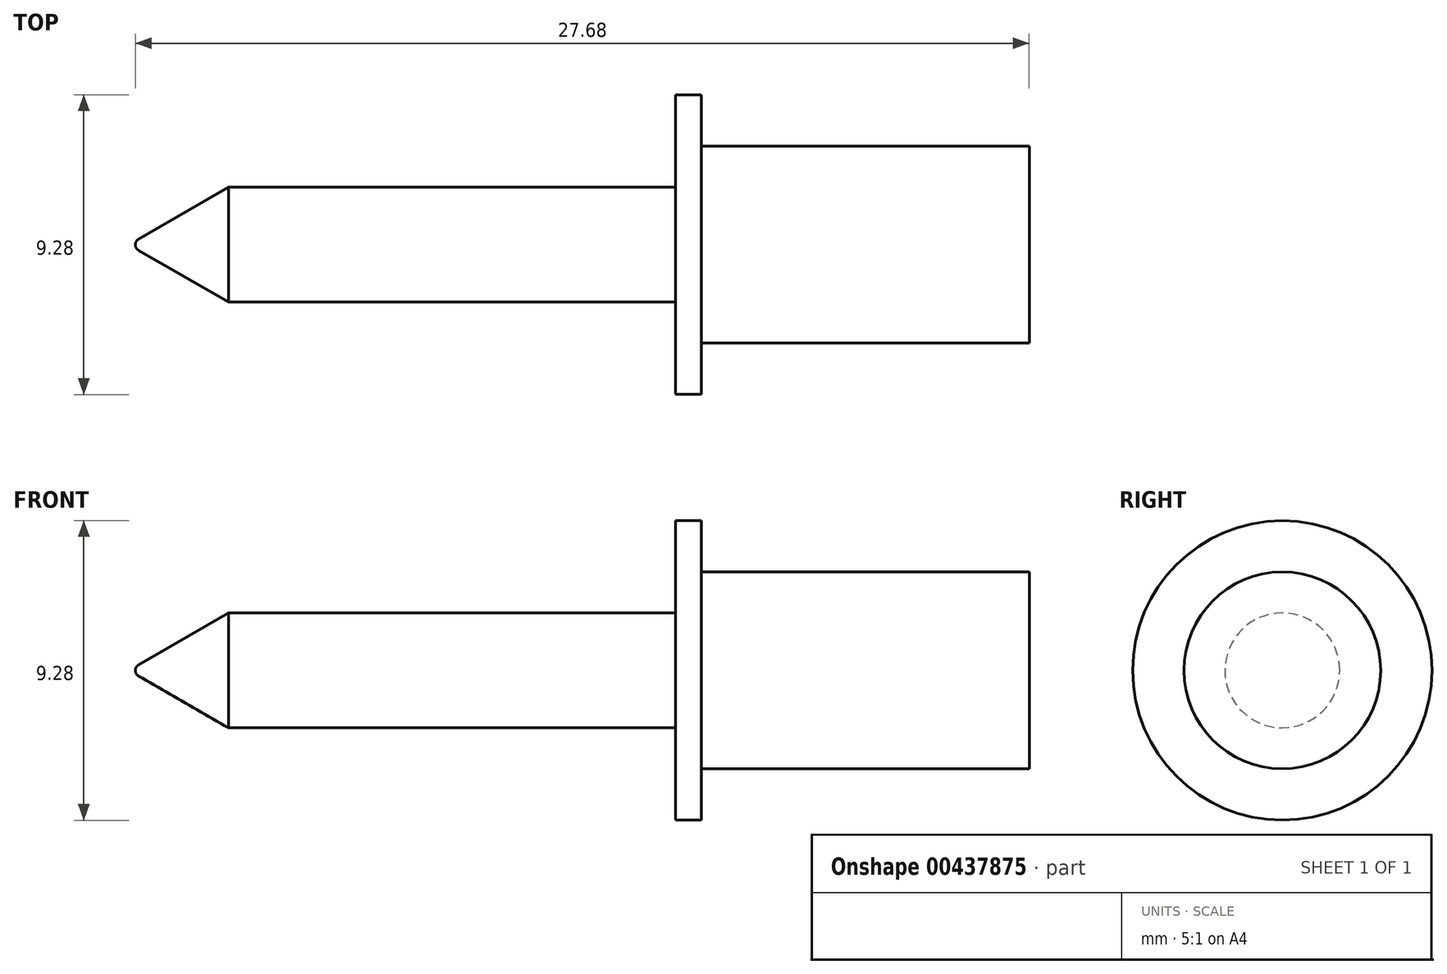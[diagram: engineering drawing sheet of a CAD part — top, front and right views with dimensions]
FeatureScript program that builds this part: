
annotation { "Feature Type Name" : "Feature", "Feature Type Description" : "" }
export const myFeature = defineFeature(function(context is Context, id is Id, definition is map)
    precondition{}
    {
        {
            var Q0;
            Q0=qCreatedBy(makeId("Front.planeOp"),FACE);
            var sketch = newSketch(context, id + "F0", { "sketchPlane" : qUnion([Q0])});
            skLineSegment(sketch, "E0", {"start": v(13.84, 0) * mm, "end": v(-13.84, 0) * mm, "construction": true});
            skSolve(sketch);
        }
        {
            var Q0;
            Q0=qCreatedBy(makeId("Front.planeOp"),FACE);
            var sketch = newSketch(context, id + "F1", { "sketchPlane" : qUnion([Q0])});
            skLineSegment(sketch, "E1.0", {"start": v(13.84, 0) * mm, "end": v(-13.84, 0) * mm});
            skLineSegment(sketch, "E2.0", {"start": v(2.89, 1.78) * mm, "end": v(-10.96, 1.78) * mm});
            skLineSegment(sketch, "E3.0", {"start": v(13.84, 3.05) * mm, "end": v(3.68, 3.05) * mm});
            skLineSegment(sketch, "E4", {"start": v(13.84, 3.05) * mm, "end": v(13.84, 0) * mm});
            skLineSegment(sketch, "E5", {"start": v(3.68, 4.64) * mm, "end": v(3.68, 3.05) * mm});
            skLineSegment(sketch, "E6.0", {"start": v(2.89, 4.64) * mm, "end": v(2.89, 1.78) * mm});
            skLineSegment(sketch, "E7.0", {"start": v(3.68, 4.64) * mm, "end": v(2.89, 4.64) * mm});
            skLineSegment(sketch, "E8", {"start": v(-10.96, 1.78) * mm, "end": v(-13.74, 0.17) * mm});
            skArc(sketch, "E9", {"start": v(-13.74, 0.17) * mm, "mid": v(-13.82, 0.1) * mm, "end": v(-13.84, 0) * mm});
            skSolve(sketch);
        }
        {
            var Q0;
            Q0=makeQuery(id+"F1.imprint","IMPRINT",FACE,{"disambiguationData":[TD([[makeQuery(id+"F1.imprint","IMPRINT",EDGE,{"derivedFrom":sQuery(id+"F1.wireOp",EDGE,"E1.0")}),-1.0]])]});
            var Q1;
            Q1=sQuery(id+"F0.wireOp",EDGE,"E0");
            revolve(context, id + "F2", {"entities" : qUnion([Q0]), "axis" : qUnion([Q1]), "revolveType" : RevolveType.FULL});
        }
    });
